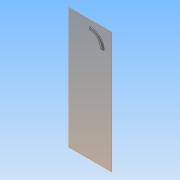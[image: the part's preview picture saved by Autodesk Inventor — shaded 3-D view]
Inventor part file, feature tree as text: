
AUTODESK INVENTOR PART (.ipt)
format: ipt  version: 2013 (Build 170138000, 138)  size: 108,032 bytes
history: native  units: in
note: dims shown in document units (in); Inventor stores cm internally (conversion verified against a paired STEP export)
features: reference x4, extrude x2, sketch x2, plane x1
ambient origin geometry x8: Origin, YZ Plane, XZ Plane, XY Plane, X Axis, Y Axis, Z Axis, Center Point
bodies: Solid1 (feature_tree)
feature tree (9):
  plane  "Work Plane1"
  extrude  "Extrusion1"  Depth=0.71in TaperAngle=0.0deg
  extrude  "Extrusion2"  Depth=0.5in TaperAngle=0.0deg
  sketch  "Sketch1"  dims[d0=12.0in d1=0.71in d2=0.0in]
  reference  "Reference1"
  reference  "Reference2"
  reference  "Reference3"
  sketch  "Sketch2"  dims[d3=0.5in d5=0.5in d6=0.0in]
  reference  "Reference4"
